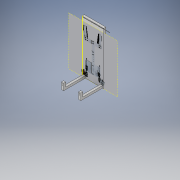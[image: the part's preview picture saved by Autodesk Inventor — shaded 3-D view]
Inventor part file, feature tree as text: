
AUTODESK INVENTOR PART (.ipt)
format: ipt  version: 2018 (Build 220112000, 112)  size: 3,213,824 bytes
history: native  units: in
note: dims shown in document units (in); Inventor stores cm internally (conversion verified against a paired STEP export)
features: sketch x6, extrude x5, other x1
ambient origin geometry x8: Origin, YZ Plane, XZ Plane, XY Plane, X Axis, Y Axis, Z Axis, Center Point
bodies: Solid1 (feature_tree)
feature tree (12):
  extrude  "Extrusion1"  Depth=24.0in
  extrude  "Extrusion2"  Depth=1.0in
  extrude  "Extrusion3"  Depth=0.5in
  extrude  "Extrusion4"  Depth=1.0in
  sketch  "Sketch5"  dims[d9=10.0in d10=0.0in d11=1.0in]
  extrude  "Extrusion5"  Depth=1.0in
  sketch  "Sketch1"  dims[d0=9.874in d1=24.0in]
  sketch  "Sketch2"  dims[d2=1.0in d3=0.0in d4=1.0in]
  sketch  "Sketch3"  dims[d5=1.0in d6=0.5in]
  sketch  "Sketch4"  dims[d7=1.0in d8=1.0in]
  other  "Image1"
  sketch  "Sketch6"  dims[d12=1.0in d13=2.0in d14=0.0in d15=0.5in d16=0.5in d17=0.2031in d18=2.0in d19=0.0in d33=0.01in d34=0.0in]
